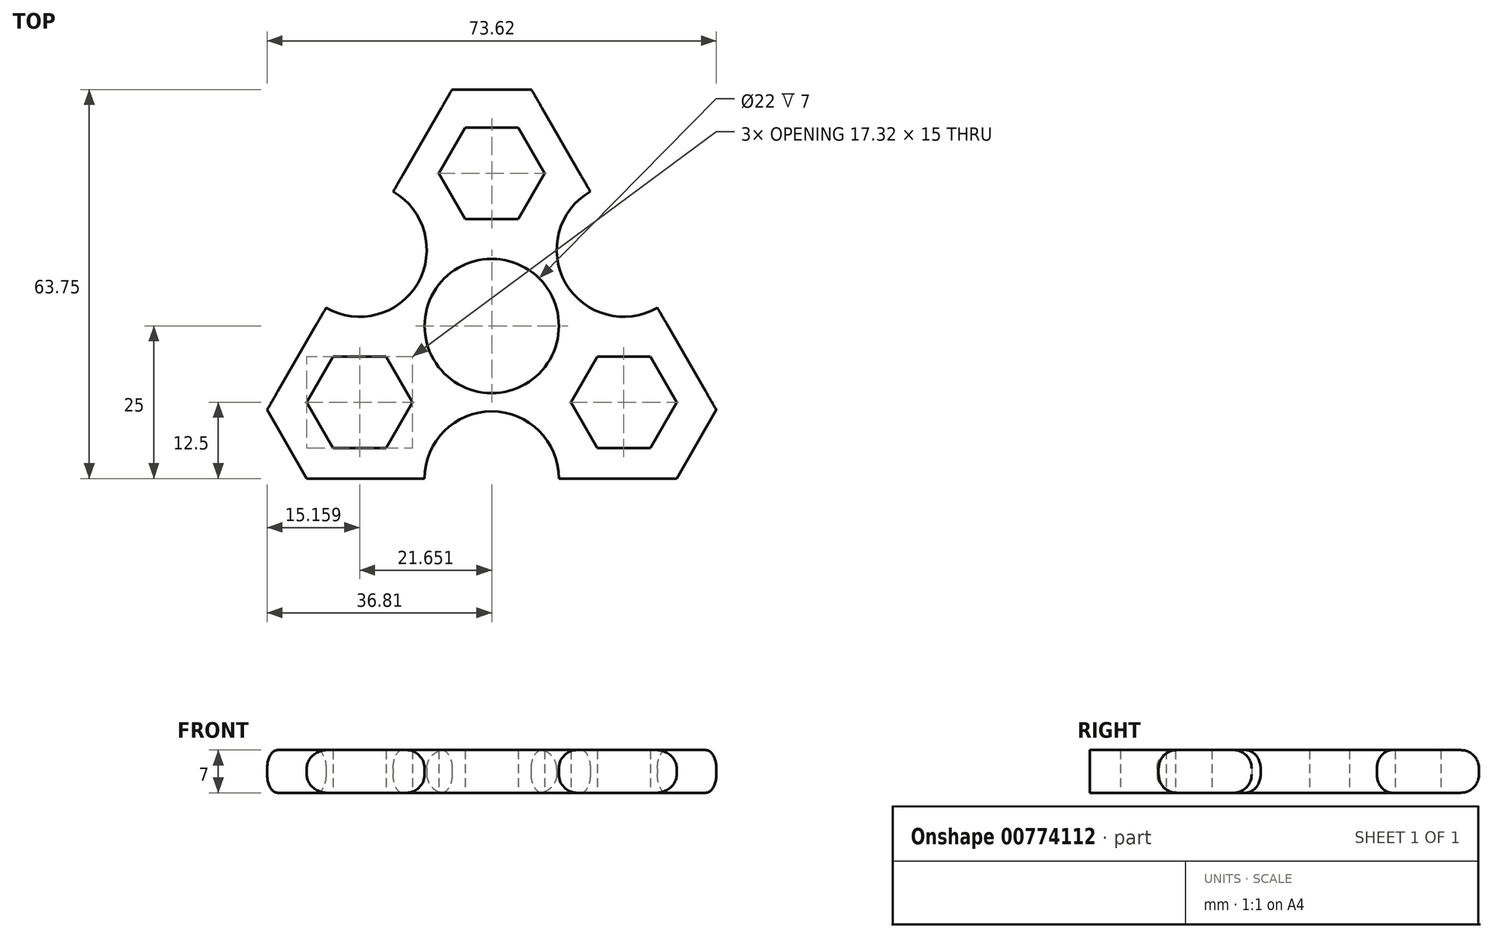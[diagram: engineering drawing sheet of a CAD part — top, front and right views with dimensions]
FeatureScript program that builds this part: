
annotation { "Feature Type Name" : "Feature", "Feature Type Description" : "" }
export const myFeature = defineFeature(function(context is Context, id is Id, definition is map)
    precondition{}
    {
        {
            var Q0;
            Q0=qCreatedBy(makeId("Top.planeOp"),FACE);
            var sketch = newSketch(context, id + "F0", { "sketchPlane" : qUnion([Q0])});
            skPoint(sketch, "E0", {"position": v(0, 0) * mm});
            skCircle(sketch, "E1", {"center": v(0, 0) * mm, "radius": 11 * mm});
            skCircle(sketch, "E2.cCircle", {"center": v(0, 0) * mm, "radius": 25 * mm, "construction": true});
            skLineSegment(sketch, "E2.0", {"start": v(43.3, -25) * mm, "end": v(-43.3, -25) * mm});
            skLineSegment(sketch, "E2.1", {"start": v(-43.3, -25) * mm, "end": v(0, 50) * mm});
            skLineSegment(sketch, "E2.2", {"start": v(0, 50) * mm, "end": v(43.3, -25) * mm});
            skPoint(sketch, "E2.0.midPoint", {"position": v(0, -25) * mm});
            skLineSegment(sketch, "E3", {"start": v(-43.3, -25) * mm, "end": v(0, 0) * mm});
            skLineSegment(sketch, "E4", {"start": v(0, 0) * mm, "end": v(43.3, -25) * mm});
            skLineSegment(sketch, "E5", {"start": v(0, 0) * mm, "end": v(0, 50) * mm});
            skCircle(sketch, "E6", {"center": v(-21.65, 12.5) * mm, "radius": 11 * mm});
            skCircle(sketch, "E7", {"center": v(21.65, 12.5) * mm, "radius": 11 * mm});
            skCircle(sketch, "E8", {"center": v(0, -25) * mm, "radius": 11 * mm});
            skLineSegment(sketch, "E9.0", {"start": v(25.98, -20) * mm, "end": v(17.32, -20) * mm});
            skLineSegment(sketch, "E9.1", {"start": v(17.32, -20) * mm, "end": v(13, -12.5) * mm});
            skLineSegment(sketch, "E9.2", {"start": v(13, -12.5) * mm, "end": v(17.32, -5) * mm});
            skLineSegment(sketch, "E9.3", {"start": v(17.32, -5) * mm, "end": v(25.98, -5) * mm});
            skLineSegment(sketch, "E9.4", {"start": v(25.98, -5) * mm, "end": v(30.31, -12.5) * mm});
            skLineSegment(sketch, "E9.5", {"start": v(30.31, -12.5) * mm, "end": v(25.98, -20) * mm});
            skPoint(sketch, "E10", {"position": v(21.65, -12.5) * mm});
            skPoint(sketch, "E10.positionSnap0", {"position": v(21.65, -20) * mm});
            skPoint(sketch, "E11", {"position": v(0, 25) * mm});
            skPoint(sketch, "E12", {"position": v(-21.65, -12.5) * mm});
            skLineSegment(sketch, "E13.0", {"start": v(4.33, 17.5) * mm, "end": v(-4.33, 17.5) * mm});
            skLineSegment(sketch, "E13.1", {"start": v(-4.33, 17.5) * mm, "end": v(-8.66, 25) * mm});
            skLineSegment(sketch, "E13.2", {"start": v(-8.66, 25) * mm, "end": v(-4.33, 32.5) * mm});
            skLineSegment(sketch, "E13.3", {"start": v(-4.33, 32.5) * mm, "end": v(4.33, 32.5) * mm});
            skLineSegment(sketch, "E13.4", {"start": v(4.33, 32.5) * mm, "end": v(8.66, 25) * mm});
            skLineSegment(sketch, "E13.5", {"start": v(8.66, 25) * mm, "end": v(4.33, 17.5) * mm});
            skPoint(sketch, "E13.0.midPoint", {"position": v(0, 17.5) * mm});
            skPoint(sketch, "E14.MirrorP", {"position": v(-21.65, -20) * mm});
            skLineSegment(sketch, "E15.MirrorCS", {"start": v(-25.98, -20) * mm, "end": v(-17.32, -20) * mm});
            skLineSegment(sketch, "E16.MirrorCS", {"start": v(-30.31, -12.5) * mm, "end": v(-25.98, -20) * mm});
            skLineSegment(sketch, "E17.MirrorCS", {"start": v(-25.98, -5) * mm, "end": v(-30.31, -12.5) * mm});
            skLineSegment(sketch, "E18.MirrorCS", {"start": v(-17.32, -5) * mm, "end": v(-25.98, -5) * mm});
            skLineSegment(sketch, "E19.MirrorCS", {"start": v(-13, -12.5) * mm, "end": v(-17.32, -5) * mm});
            skLineSegment(sketch, "E20.MirrorCS", {"start": v(-17.32, -20) * mm, "end": v(-13, -12.5) * mm});
            skCircle(sketch, "E21", {"center": v(0, 25) * mm, "radius": 7.5 * mm});
            skSolve(sketch);
        }
        {
            var Q0;
            {var subQ8=sQuery(id+"F0.wireOp",EDGE,"E3");var subQ11=sQuery(id+"F0.wireOp",EDGE,"E1");var subQ12=makeQuery(id+"F0.imprint","INTERSECT",VERTEX,{"derivedFrom":[subQ11,subQ8]});Q0=makeQuery(id+"F0.imprint","IMPRINT",FACE,{"disambiguationData":[TD([[makeQuery(id+"F0.imprint","IMPRINT",EDGE,{"disambiguationData":[TD([[subQ12,1.0]])],"derivedFrom":subQ11}),-1.0]])]});}
            var Q1;
            {var subQ0=sQuery(id+"F0.wireOp",EDGE,"E5");var subQ4=sQuery(id+"F0.wireOp",EDGE,"E1");var subQ5=makeQuery(id+"F0.imprint","INTERSECT",VERTEX,{"derivedFrom":[subQ4,subQ0]});Q1=makeQuery(id+"F0.imprint","IMPRINT",FACE,{"disambiguationData":[TD([[makeQuery(id+"F0.imprint","IMPRINT",EDGE,{"disambiguationData":[TD([[subQ5,1.0]])],"derivedFrom":subQ4}),-1.0]])]});}
            var Q2;
            {var subQ8=sQuery(id+"F0.wireOp",EDGE,"E3");var subQ11=sQuery(id+"F0.wireOp",EDGE,"E1");var subQ12=makeQuery(id+"F0.imprint","INTERSECT",VERTEX,{"derivedFrom":[subQ11,subQ8]});Q2=makeQuery(id+"F0.imprint","IMPRINT",FACE,{"disambiguationData":[TD([[makeQuery(id+"F0.imprint","IMPRINT",EDGE,{"disambiguationData":[TD([[subQ12,-1.0]])],"derivedFrom":subQ11}),-1.0]])]});}
            extrude(context, id + "F1", {"entities" : qUnion([Q0, Q1, Q2]), "depth" : 3.5 * mm, "offsetDistance" : 25 * mm, "hasSecondDirection" : true, "secondDirectionOppositeDirection" : true, "secondDirectionDepth" : 3.5 * mm});
        }
        {
            var Q0;
            Q0=makeQuery(id+"F1.opExtrude","SWEPT_EDGE",EDGE,{"disambiguationData":[OSD([sQuery(id+"F0.wireOp",EDGE,"E2.1"),sQuery(id+"F0.wireOp",EDGE,"E2.2"),sQuery(id+"F0.wireOp",EDGE,"E5")])]});
            var Q1;
            Q1=makeQuery(id+"F1.opExtrude","SWEPT_EDGE",EDGE,{"disambiguationData":[OSD([sQuery(id+"F0.wireOp",EDGE,"E2.0"),sQuery(id+"F0.wireOp",EDGE,"E2.2"),sQuery(id+"F0.wireOp",EDGE,"E4")])]});
            var Q2;
            Q2=makeQuery(id+"F1.opExtrude","SWEPT_EDGE",EDGE,{"disambiguationData":[OSD([sQuery(id+"F0.wireOp",EDGE,"E2.0"),sQuery(id+"F0.wireOp",EDGE,"E2.1"),sQuery(id+"F0.wireOp",EDGE,"E3")])]});
            chamfer(context, id + "F2", {"entities" : qUnion([Q0, Q1, Q2]), "width" : 7.5 * mm, "tangentPropagation" : true});
        }
        {
            var Q0;
            {var subQ0=sQuery(id+"F0.wireOp",EDGE,"E2.2");Q0=makeQuery(id+"F1.opExtrude","CAP_EDGE",EDGE,{"disambiguationData":[OSD([subQ0]),TDD([makeQuery(id+"F0.imprint","IMPRINT",EDGE,{"disambiguationData":[TD([[makeQuery(id+"F0.imprint","INTERSECT",VERTEX,{"disambiguationData":[OD(0.0)],"derivedFrom":[subQ0,sQuery(id+"F0.wireOp",EDGE,"E7")]}),1.0]])],"derivedFrom":subQ0})])],"isStart":false});}
            var Q1;
            Q1=makeQuery(id+"F1.opExtrude","CAP_EDGE",EDGE,{"disambiguationData":[OSD([sQuery(id+"F0.wireOp",EDGE,"E7")])],"isStart":false});
            var Q2;
            {var subQ0=sQuery(id+"F0.wireOp",EDGE,"E2.2");Q2=makeQuery(id+"F1.opExtrude","CAP_EDGE",EDGE,{"disambiguationData":[OSD([subQ0]),TDD([makeQuery(id+"F0.imprint","IMPRINT",EDGE,{"disambiguationData":[TD([[makeQuery(id+"F0.imprint","INTERSECT",VERTEX,{"disambiguationData":[OD(1.0)],"derivedFrom":[subQ0,sQuery(id+"F0.wireOp",EDGE,"E7")]}),-1.0]])],"derivedFrom":subQ0})])],"isStart":false});}
            var Q3;
            {var subQ0=sQuery(id+"F0.wireOp",EDGE,"E2.2");var subQ1=sQuery(id+"F0.wireOp",EDGE,"E2.0");Q3=makeQuery(id+"F2.opChamfer","BLEND_EDGE",EDGE,{"blendedFrom":[makeQuery(id+"F1.opExtrude","SWEPT_EDGE",EDGE,{"disambiguationData":[OSD([subQ1,subQ0,sQuery(id+"F0.wireOp",EDGE,"E4")])]}),makeQuery(id+"F1.opExtrude","CAP_FACE",FACE,{"disambiguationData":[OSD([sQuery(id+"F0.wireOp",EDGE,"E1"),subQ1,sQuery(id+"F0.wireOp",EDGE,"E2.1"),subQ0,sQuery(id+"F0.wireOp",EDGE,"E6"),sQuery(id+"F0.wireOp",EDGE,"E7"),sQuery(id+"F0.wireOp",EDGE,"E8"),sQuery(id+"F0.wireOp",EDGE,"E9.0"),sQuery(id+"F0.wireOp",EDGE,"E9.1"),sQuery(id+"F0.wireOp",EDGE,"E9.2"),sQuery(id+"F0.wireOp",EDGE,"E9.3"),sQuery(id+"F0.wireOp",EDGE,"E9.4"),sQuery(id+"F0.wireOp",EDGE,"E9.5"),sQuery(id+"F0.wireOp",EDGE,"E13.0"),sQuery(id+"F0.wireOp",EDGE,"E13.1"),sQuery(id+"F0.wireOp",EDGE,"E13.2"),sQuery(id+"F0.wireOp",EDGE,"E13.3"),sQuery(id+"F0.wireOp",EDGE,"E13.4"),sQuery(id+"F0.wireOp",EDGE,"E13.5"),sQuery(id+"F0.wireOp",EDGE,"E15.MirrorCS"),sQuery(id+"F0.wireOp",EDGE,"E16.MirrorCS"),sQuery(id+"F0.wireOp",EDGE,"E17.MirrorCS"),sQuery(id+"F0.wireOp",EDGE,"E18.MirrorCS"),sQuery(id+"F0.wireOp",EDGE,"E19.MirrorCS"),sQuery(id+"F0.wireOp",EDGE,"E20.MirrorCS")])],"isStart":false})],"blendedInto":[makeQuery(id+"F1.opExtrude","CAP_FACE",FACE,{"disambiguationData":[OSD([sQuery(id+"F0.wireOp",EDGE,"E1"),subQ1,sQuery(id+"F0.wireOp",EDGE,"E2.1"),subQ0,sQuery(id+"F0.wireOp",EDGE,"E6"),sQuery(id+"F0.wireOp",EDGE,"E7"),sQuery(id+"F0.wireOp",EDGE,"E8"),sQuery(id+"F0.wireOp",EDGE,"E9.0"),sQuery(id+"F0.wireOp",EDGE,"E9.1"),sQuery(id+"F0.wireOp",EDGE,"E9.2"),sQuery(id+"F0.wireOp",EDGE,"E9.3"),sQuery(id+"F0.wireOp",EDGE,"E9.4"),sQuery(id+"F0.wireOp",EDGE,"E9.5"),sQuery(id+"F0.wireOp",EDGE,"E13.0"),sQuery(id+"F0.wireOp",EDGE,"E13.1"),sQuery(id+"F0.wireOp",EDGE,"E13.2"),sQuery(id+"F0.wireOp",EDGE,"E13.3"),sQuery(id+"F0.wireOp",EDGE,"E13.4"),sQuery(id+"F0.wireOp",EDGE,"E13.5"),sQuery(id+"F0.wireOp",EDGE,"E15.MirrorCS"),sQuery(id+"F0.wireOp",EDGE,"E16.MirrorCS"),sQuery(id+"F0.wireOp",EDGE,"E17.MirrorCS"),sQuery(id+"F0.wireOp",EDGE,"E18.MirrorCS"),sQuery(id+"F0.wireOp",EDGE,"E19.MirrorCS"),sQuery(id+"F0.wireOp",EDGE,"E20.MirrorCS")])],"isStart":false})]});}
            var Q4;
            {var subQ0=sQuery(id+"F0.wireOp",EDGE,"E2.0");Q4=makeQuery(id+"F1.opExtrude","CAP_EDGE",EDGE,{"disambiguationData":[OSD([subQ0]),TDD([makeQuery(id+"F0.imprint","IMPRINT",EDGE,{"disambiguationData":[TD([[makeQuery(id+"F0.imprint","INTERSECT",VERTEX,{"disambiguationData":[OD(0.0)],"derivedFrom":[subQ0,sQuery(id+"F0.wireOp",EDGE,"E8")]}),1.0]])],"derivedFrom":subQ0})])],"isStart":false});}
            var Q5;
            Q5=makeQuery(id+"F1.opExtrude","CAP_EDGE",EDGE,{"disambiguationData":[OSD([sQuery(id+"F0.wireOp",EDGE,"E8")])],"isStart":false});
            var Q6;
            {var subQ0=sQuery(id+"F0.wireOp",EDGE,"E2.0");Q6=makeQuery(id+"F1.opExtrude","CAP_EDGE",EDGE,{"disambiguationData":[OSD([subQ0]),TDD([makeQuery(id+"F0.imprint","IMPRINT",EDGE,{"disambiguationData":[TD([[makeQuery(id+"F0.imprint","INTERSECT",VERTEX,{"disambiguationData":[OD(1.0)],"derivedFrom":[subQ0,sQuery(id+"F0.wireOp",EDGE,"E8")]}),-1.0]])],"derivedFrom":subQ0})])],"isStart":false});}
            var Q7;
            {var subQ0=sQuery(id+"F0.wireOp",EDGE,"E2.1");var subQ1=sQuery(id+"F0.wireOp",EDGE,"E2.0");Q7=makeQuery(id+"F2.opChamfer","BLEND_EDGE",EDGE,{"blendedFrom":[makeQuery(id+"F1.opExtrude","SWEPT_EDGE",EDGE,{"disambiguationData":[OSD([subQ1,subQ0,sQuery(id+"F0.wireOp",EDGE,"E3")])]}),makeQuery(id+"F1.opExtrude","CAP_FACE",FACE,{"disambiguationData":[OSD([sQuery(id+"F0.wireOp",EDGE,"E1"),subQ1,subQ0,sQuery(id+"F0.wireOp",EDGE,"E2.2"),sQuery(id+"F0.wireOp",EDGE,"E6"),sQuery(id+"F0.wireOp",EDGE,"E7"),sQuery(id+"F0.wireOp",EDGE,"E8"),sQuery(id+"F0.wireOp",EDGE,"E9.0"),sQuery(id+"F0.wireOp",EDGE,"E9.1"),sQuery(id+"F0.wireOp",EDGE,"E9.2"),sQuery(id+"F0.wireOp",EDGE,"E9.3"),sQuery(id+"F0.wireOp",EDGE,"E9.4"),sQuery(id+"F0.wireOp",EDGE,"E9.5"),sQuery(id+"F0.wireOp",EDGE,"E13.0"),sQuery(id+"F0.wireOp",EDGE,"E13.1"),sQuery(id+"F0.wireOp",EDGE,"E13.2"),sQuery(id+"F0.wireOp",EDGE,"E13.3"),sQuery(id+"F0.wireOp",EDGE,"E13.4"),sQuery(id+"F0.wireOp",EDGE,"E13.5"),sQuery(id+"F0.wireOp",EDGE,"E15.MirrorCS"),sQuery(id+"F0.wireOp",EDGE,"E16.MirrorCS"),sQuery(id+"F0.wireOp",EDGE,"E17.MirrorCS"),sQuery(id+"F0.wireOp",EDGE,"E18.MirrorCS"),sQuery(id+"F0.wireOp",EDGE,"E19.MirrorCS"),sQuery(id+"F0.wireOp",EDGE,"E20.MirrorCS")])],"isStart":false})],"blendedInto":[makeQuery(id+"F1.opExtrude","CAP_FACE",FACE,{"disambiguationData":[OSD([sQuery(id+"F0.wireOp",EDGE,"E1"),subQ1,subQ0,sQuery(id+"F0.wireOp",EDGE,"E2.2"),sQuery(id+"F0.wireOp",EDGE,"E6"),sQuery(id+"F0.wireOp",EDGE,"E7"),sQuery(id+"F0.wireOp",EDGE,"E8"),sQuery(id+"F0.wireOp",EDGE,"E9.0"),sQuery(id+"F0.wireOp",EDGE,"E9.1"),sQuery(id+"F0.wireOp",EDGE,"E9.2"),sQuery(id+"F0.wireOp",EDGE,"E9.3"),sQuery(id+"F0.wireOp",EDGE,"E9.4"),sQuery(id+"F0.wireOp",EDGE,"E9.5"),sQuery(id+"F0.wireOp",EDGE,"E13.0"),sQuery(id+"F0.wireOp",EDGE,"E13.1"),sQuery(id+"F0.wireOp",EDGE,"E13.2"),sQuery(id+"F0.wireOp",EDGE,"E13.3"),sQuery(id+"F0.wireOp",EDGE,"E13.4"),sQuery(id+"F0.wireOp",EDGE,"E13.5"),sQuery(id+"F0.wireOp",EDGE,"E15.MirrorCS"),sQuery(id+"F0.wireOp",EDGE,"E16.MirrorCS"),sQuery(id+"F0.wireOp",EDGE,"E17.MirrorCS"),sQuery(id+"F0.wireOp",EDGE,"E18.MirrorCS"),sQuery(id+"F0.wireOp",EDGE,"E19.MirrorCS"),sQuery(id+"F0.wireOp",EDGE,"E20.MirrorCS")])],"isStart":false})]});}
            var Q8;
            {var subQ0=sQuery(id+"F0.wireOp",EDGE,"E2.1");Q8=makeQuery(id+"F1.opExtrude","CAP_EDGE",EDGE,{"disambiguationData":[OSD([subQ0]),TDD([makeQuery(id+"F0.imprint","IMPRINT",EDGE,{"disambiguationData":[TD([[makeQuery(id+"F0.imprint","INTERSECT",VERTEX,{"disambiguationData":[OD(0.0)],"derivedFrom":[subQ0,sQuery(id+"F0.wireOp",EDGE,"E6")]}),1.0]])],"derivedFrom":subQ0})])],"isStart":false});}
            var Q9;
            Q9=makeQuery(id+"F1.opExtrude","CAP_EDGE",EDGE,{"disambiguationData":[OSD([sQuery(id+"F0.wireOp",EDGE,"E6")])],"isStart":false});
            var Q10;
            {var subQ0=sQuery(id+"F0.wireOp",EDGE,"E2.1");Q10=makeQuery(id+"F1.opExtrude","CAP_EDGE",EDGE,{"disambiguationData":[OSD([subQ0]),TDD([makeQuery(id+"F0.imprint","IMPRINT",EDGE,{"disambiguationData":[TD([[makeQuery(id+"F0.imprint","INTERSECT",VERTEX,{"disambiguationData":[OD(1.0)],"derivedFrom":[subQ0,sQuery(id+"F0.wireOp",EDGE,"E6")]}),-1.0]])],"derivedFrom":subQ0})])],"isStart":false});}
            var Q11;
            {var subQ0=sQuery(id+"F0.wireOp",EDGE,"E2.2");var subQ1=sQuery(id+"F0.wireOp",EDGE,"E2.1");Q11=makeQuery(id+"F2.opChamfer","BLEND_EDGE",EDGE,{"blendedFrom":[makeQuery(id+"F1.opExtrude","SWEPT_EDGE",EDGE,{"disambiguationData":[OSD([subQ1,subQ0,sQuery(id+"F0.wireOp",EDGE,"E5")])]}),makeQuery(id+"F1.opExtrude","CAP_FACE",FACE,{"disambiguationData":[OSD([sQuery(id+"F0.wireOp",EDGE,"E1"),sQuery(id+"F0.wireOp",EDGE,"E2.0"),subQ1,subQ0,sQuery(id+"F0.wireOp",EDGE,"E6"),sQuery(id+"F0.wireOp",EDGE,"E7"),sQuery(id+"F0.wireOp",EDGE,"E8"),sQuery(id+"F0.wireOp",EDGE,"E9.0"),sQuery(id+"F0.wireOp",EDGE,"E9.1"),sQuery(id+"F0.wireOp",EDGE,"E9.2"),sQuery(id+"F0.wireOp",EDGE,"E9.3"),sQuery(id+"F0.wireOp",EDGE,"E9.4"),sQuery(id+"F0.wireOp",EDGE,"E9.5"),sQuery(id+"F0.wireOp",EDGE,"E13.0"),sQuery(id+"F0.wireOp",EDGE,"E13.1"),sQuery(id+"F0.wireOp",EDGE,"E13.2"),sQuery(id+"F0.wireOp",EDGE,"E13.3"),sQuery(id+"F0.wireOp",EDGE,"E13.4"),sQuery(id+"F0.wireOp",EDGE,"E13.5"),sQuery(id+"F0.wireOp",EDGE,"E15.MirrorCS"),sQuery(id+"F0.wireOp",EDGE,"E16.MirrorCS"),sQuery(id+"F0.wireOp",EDGE,"E17.MirrorCS"),sQuery(id+"F0.wireOp",EDGE,"E18.MirrorCS"),sQuery(id+"F0.wireOp",EDGE,"E19.MirrorCS"),sQuery(id+"F0.wireOp",EDGE,"E20.MirrorCS")])],"isStart":false})],"blendedInto":[makeQuery(id+"F1.opExtrude","CAP_FACE",FACE,{"disambiguationData":[OSD([sQuery(id+"F0.wireOp",EDGE,"E1"),sQuery(id+"F0.wireOp",EDGE,"E2.0"),subQ1,subQ0,sQuery(id+"F0.wireOp",EDGE,"E6"),sQuery(id+"F0.wireOp",EDGE,"E7"),sQuery(id+"F0.wireOp",EDGE,"E8"),sQuery(id+"F0.wireOp",EDGE,"E9.0"),sQuery(id+"F0.wireOp",EDGE,"E9.1"),sQuery(id+"F0.wireOp",EDGE,"E9.2"),sQuery(id+"F0.wireOp",EDGE,"E9.3"),sQuery(id+"F0.wireOp",EDGE,"E9.4"),sQuery(id+"F0.wireOp",EDGE,"E9.5"),sQuery(id+"F0.wireOp",EDGE,"E13.0"),sQuery(id+"F0.wireOp",EDGE,"E13.1"),sQuery(id+"F0.wireOp",EDGE,"E13.2"),sQuery(id+"F0.wireOp",EDGE,"E13.3"),sQuery(id+"F0.wireOp",EDGE,"E13.4"),sQuery(id+"F0.wireOp",EDGE,"E13.5"),sQuery(id+"F0.wireOp",EDGE,"E15.MirrorCS"),sQuery(id+"F0.wireOp",EDGE,"E16.MirrorCS"),sQuery(id+"F0.wireOp",EDGE,"E17.MirrorCS"),sQuery(id+"F0.wireOp",EDGE,"E18.MirrorCS"),sQuery(id+"F0.wireOp",EDGE,"E19.MirrorCS"),sQuery(id+"F0.wireOp",EDGE,"E20.MirrorCS")])],"isStart":false})]});}
            fillet(context, id + "F3", {"entities" : qUnion([Q0, Q1, Q2, Q3, Q4, Q5, Q6, Q7, Q8, Q9, Q10, Q11]), "radius" : 3 * mm, "tangentPropagation" : true, "allowEdgeOverflow" : false});
        }
        {
            var Q0;
            {var subQ0=sQuery(id+"F0.wireOp",EDGE,"E2.1");var subQ1=sQuery(id+"F0.wireOp",EDGE,"E2.0");Q0=makeQuery(id+"F2.opChamfer","BLEND_EDGE",EDGE,{"blendedFrom":[makeQuery(id+"F1.opExtrude","SWEPT_EDGE",EDGE,{"disambiguationData":[OSD([subQ1,subQ0,sQuery(id+"F0.wireOp",EDGE,"E3")])]}),makeQuery(id+"F1.opExtrude","CAP_FACE",FACE,{"disambiguationData":[OSD([sQuery(id+"F0.wireOp",EDGE,"E1"),subQ1,subQ0,sQuery(id+"F0.wireOp",EDGE,"E2.2"),sQuery(id+"F0.wireOp",EDGE,"E6"),sQuery(id+"F0.wireOp",EDGE,"E7"),sQuery(id+"F0.wireOp",EDGE,"E8"),sQuery(id+"F0.wireOp",EDGE,"E9.0"),sQuery(id+"F0.wireOp",EDGE,"E9.1"),sQuery(id+"F0.wireOp",EDGE,"E9.2"),sQuery(id+"F0.wireOp",EDGE,"E9.3"),sQuery(id+"F0.wireOp",EDGE,"E9.4"),sQuery(id+"F0.wireOp",EDGE,"E9.5"),sQuery(id+"F0.wireOp",EDGE,"E13.0"),sQuery(id+"F0.wireOp",EDGE,"E13.1"),sQuery(id+"F0.wireOp",EDGE,"E13.2"),sQuery(id+"F0.wireOp",EDGE,"E13.3"),sQuery(id+"F0.wireOp",EDGE,"E13.4"),sQuery(id+"F0.wireOp",EDGE,"E13.5"),sQuery(id+"F0.wireOp",EDGE,"E15.MirrorCS"),sQuery(id+"F0.wireOp",EDGE,"E16.MirrorCS"),sQuery(id+"F0.wireOp",EDGE,"E17.MirrorCS"),sQuery(id+"F0.wireOp",EDGE,"E18.MirrorCS"),sQuery(id+"F0.wireOp",EDGE,"E19.MirrorCS"),sQuery(id+"F0.wireOp",EDGE,"E20.MirrorCS")])],"isStart":true})],"blendedInto":[makeQuery(id+"F1.opExtrude","CAP_FACE",FACE,{"disambiguationData":[OSD([sQuery(id+"F0.wireOp",EDGE,"E1"),subQ1,subQ0,sQuery(id+"F0.wireOp",EDGE,"E2.2"),sQuery(id+"F0.wireOp",EDGE,"E6"),sQuery(id+"F0.wireOp",EDGE,"E7"),sQuery(id+"F0.wireOp",EDGE,"E8"),sQuery(id+"F0.wireOp",EDGE,"E9.0"),sQuery(id+"F0.wireOp",EDGE,"E9.1"),sQuery(id+"F0.wireOp",EDGE,"E9.2"),sQuery(id+"F0.wireOp",EDGE,"E9.3"),sQuery(id+"F0.wireOp",EDGE,"E9.4"),sQuery(id+"F0.wireOp",EDGE,"E9.5"),sQuery(id+"F0.wireOp",EDGE,"E13.0"),sQuery(id+"F0.wireOp",EDGE,"E13.1"),sQuery(id+"F0.wireOp",EDGE,"E13.2"),sQuery(id+"F0.wireOp",EDGE,"E13.3"),sQuery(id+"F0.wireOp",EDGE,"E13.4"),sQuery(id+"F0.wireOp",EDGE,"E13.5"),sQuery(id+"F0.wireOp",EDGE,"E15.MirrorCS"),sQuery(id+"F0.wireOp",EDGE,"E16.MirrorCS"),sQuery(id+"F0.wireOp",EDGE,"E17.MirrorCS"),sQuery(id+"F0.wireOp",EDGE,"E18.MirrorCS"),sQuery(id+"F0.wireOp",EDGE,"E19.MirrorCS"),sQuery(id+"F0.wireOp",EDGE,"E20.MirrorCS")])],"isStart":true})]});}
            var Q1;
            {var subQ0=sQuery(id+"F0.wireOp",EDGE,"E2.2");var subQ1=sQuery(id+"F0.wireOp",EDGE,"E2.0");Q1=makeQuery(id+"F2.opChamfer","BLEND_EDGE",EDGE,{"blendedFrom":[makeQuery(id+"F1.opExtrude","SWEPT_EDGE",EDGE,{"disambiguationData":[OSD([subQ1,subQ0,sQuery(id+"F0.wireOp",EDGE,"E4")])]}),makeQuery(id+"F1.opExtrude","CAP_FACE",FACE,{"disambiguationData":[OSD([sQuery(id+"F0.wireOp",EDGE,"E1"),subQ1,sQuery(id+"F0.wireOp",EDGE,"E2.1"),subQ0,sQuery(id+"F0.wireOp",EDGE,"E6"),sQuery(id+"F0.wireOp",EDGE,"E7"),sQuery(id+"F0.wireOp",EDGE,"E8"),sQuery(id+"F0.wireOp",EDGE,"E9.0"),sQuery(id+"F0.wireOp",EDGE,"E9.1"),sQuery(id+"F0.wireOp",EDGE,"E9.2"),sQuery(id+"F0.wireOp",EDGE,"E9.3"),sQuery(id+"F0.wireOp",EDGE,"E9.4"),sQuery(id+"F0.wireOp",EDGE,"E9.5"),sQuery(id+"F0.wireOp",EDGE,"E13.0"),sQuery(id+"F0.wireOp",EDGE,"E13.1"),sQuery(id+"F0.wireOp",EDGE,"E13.2"),sQuery(id+"F0.wireOp",EDGE,"E13.3"),sQuery(id+"F0.wireOp",EDGE,"E13.4"),sQuery(id+"F0.wireOp",EDGE,"E13.5"),sQuery(id+"F0.wireOp",EDGE,"E15.MirrorCS"),sQuery(id+"F0.wireOp",EDGE,"E16.MirrorCS"),sQuery(id+"F0.wireOp",EDGE,"E17.MirrorCS"),sQuery(id+"F0.wireOp",EDGE,"E18.MirrorCS"),sQuery(id+"F0.wireOp",EDGE,"E19.MirrorCS"),sQuery(id+"F0.wireOp",EDGE,"E20.MirrorCS")])],"isStart":true})],"blendedInto":[makeQuery(id+"F1.opExtrude","CAP_FACE",FACE,{"disambiguationData":[OSD([sQuery(id+"F0.wireOp",EDGE,"E1"),subQ1,sQuery(id+"F0.wireOp",EDGE,"E2.1"),subQ0,sQuery(id+"F0.wireOp",EDGE,"E6"),sQuery(id+"F0.wireOp",EDGE,"E7"),sQuery(id+"F0.wireOp",EDGE,"E8"),sQuery(id+"F0.wireOp",EDGE,"E9.0"),sQuery(id+"F0.wireOp",EDGE,"E9.1"),sQuery(id+"F0.wireOp",EDGE,"E9.2"),sQuery(id+"F0.wireOp",EDGE,"E9.3"),sQuery(id+"F0.wireOp",EDGE,"E9.4"),sQuery(id+"F0.wireOp",EDGE,"E9.5"),sQuery(id+"F0.wireOp",EDGE,"E13.0"),sQuery(id+"F0.wireOp",EDGE,"E13.1"),sQuery(id+"F0.wireOp",EDGE,"E13.2"),sQuery(id+"F0.wireOp",EDGE,"E13.3"),sQuery(id+"F0.wireOp",EDGE,"E13.4"),sQuery(id+"F0.wireOp",EDGE,"E13.5"),sQuery(id+"F0.wireOp",EDGE,"E15.MirrorCS"),sQuery(id+"F0.wireOp",EDGE,"E16.MirrorCS"),sQuery(id+"F0.wireOp",EDGE,"E17.MirrorCS"),sQuery(id+"F0.wireOp",EDGE,"E18.MirrorCS"),sQuery(id+"F0.wireOp",EDGE,"E19.MirrorCS"),sQuery(id+"F0.wireOp",EDGE,"E20.MirrorCS")])],"isStart":true})]});}
            var Q2;
            {var subQ0=sQuery(id+"F0.wireOp",EDGE,"E2.2");var subQ1=sQuery(id+"F0.wireOp",EDGE,"E2.1");Q2=makeQuery(id+"F2.opChamfer","BLEND_EDGE",EDGE,{"blendedFrom":[makeQuery(id+"F1.opExtrude","SWEPT_EDGE",EDGE,{"disambiguationData":[OSD([subQ1,subQ0,sQuery(id+"F0.wireOp",EDGE,"E5")])]}),makeQuery(id+"F1.opExtrude","CAP_FACE",FACE,{"disambiguationData":[OSD([sQuery(id+"F0.wireOp",EDGE,"E1"),sQuery(id+"F0.wireOp",EDGE,"E2.0"),subQ1,subQ0,sQuery(id+"F0.wireOp",EDGE,"E6"),sQuery(id+"F0.wireOp",EDGE,"E7"),sQuery(id+"F0.wireOp",EDGE,"E8"),sQuery(id+"F0.wireOp",EDGE,"E9.0"),sQuery(id+"F0.wireOp",EDGE,"E9.1"),sQuery(id+"F0.wireOp",EDGE,"E9.2"),sQuery(id+"F0.wireOp",EDGE,"E9.3"),sQuery(id+"F0.wireOp",EDGE,"E9.4"),sQuery(id+"F0.wireOp",EDGE,"E9.5"),sQuery(id+"F0.wireOp",EDGE,"E13.0"),sQuery(id+"F0.wireOp",EDGE,"E13.1"),sQuery(id+"F0.wireOp",EDGE,"E13.2"),sQuery(id+"F0.wireOp",EDGE,"E13.3"),sQuery(id+"F0.wireOp",EDGE,"E13.4"),sQuery(id+"F0.wireOp",EDGE,"E13.5"),sQuery(id+"F0.wireOp",EDGE,"E15.MirrorCS"),sQuery(id+"F0.wireOp",EDGE,"E16.MirrorCS"),sQuery(id+"F0.wireOp",EDGE,"E17.MirrorCS"),sQuery(id+"F0.wireOp",EDGE,"E18.MirrorCS"),sQuery(id+"F0.wireOp",EDGE,"E19.MirrorCS"),sQuery(id+"F0.wireOp",EDGE,"E20.MirrorCS")])],"isStart":true})],"blendedInto":[makeQuery(id+"F1.opExtrude","CAP_FACE",FACE,{"disambiguationData":[OSD([sQuery(id+"F0.wireOp",EDGE,"E1"),sQuery(id+"F0.wireOp",EDGE,"E2.0"),subQ1,subQ0,sQuery(id+"F0.wireOp",EDGE,"E6"),sQuery(id+"F0.wireOp",EDGE,"E7"),sQuery(id+"F0.wireOp",EDGE,"E8"),sQuery(id+"F0.wireOp",EDGE,"E9.0"),sQuery(id+"F0.wireOp",EDGE,"E9.1"),sQuery(id+"F0.wireOp",EDGE,"E9.2"),sQuery(id+"F0.wireOp",EDGE,"E9.3"),sQuery(id+"F0.wireOp",EDGE,"E9.4"),sQuery(id+"F0.wireOp",EDGE,"E9.5"),sQuery(id+"F0.wireOp",EDGE,"E13.0"),sQuery(id+"F0.wireOp",EDGE,"E13.1"),sQuery(id+"F0.wireOp",EDGE,"E13.2"),sQuery(id+"F0.wireOp",EDGE,"E13.3"),sQuery(id+"F0.wireOp",EDGE,"E13.4"),sQuery(id+"F0.wireOp",EDGE,"E13.5"),sQuery(id+"F0.wireOp",EDGE,"E15.MirrorCS"),sQuery(id+"F0.wireOp",EDGE,"E16.MirrorCS"),sQuery(id+"F0.wireOp",EDGE,"E17.MirrorCS"),sQuery(id+"F0.wireOp",EDGE,"E18.MirrorCS"),sQuery(id+"F0.wireOp",EDGE,"E19.MirrorCS"),sQuery(id+"F0.wireOp",EDGE,"E20.MirrorCS")])],"isStart":true})]});}
            var Q3;
            {var subQ0=sQuery(id+"F0.wireOp",EDGE,"E2.1");Q3=makeQuery(id+"F1.opExtrude","CAP_EDGE",EDGE,{"disambiguationData":[OSD([subQ0]),TDD([makeQuery(id+"F0.imprint","IMPRINT",EDGE,{"disambiguationData":[TD([[makeQuery(id+"F0.imprint","INTERSECT",VERTEX,{"disambiguationData":[OD(1.0)],"derivedFrom":[subQ0,sQuery(id+"F0.wireOp",EDGE,"E6")]}),-1.0]])],"derivedFrom":subQ0})])],"isStart":true});}
            var Q4;
            Q4=makeQuery(id+"F1.opExtrude","CAP_EDGE",EDGE,{"disambiguationData":[OSD([sQuery(id+"F0.wireOp",EDGE,"E6")])],"isStart":true});
            var Q5;
            {var subQ0=sQuery(id+"F0.wireOp",EDGE,"E2.1");Q5=makeQuery(id+"F1.opExtrude","CAP_EDGE",EDGE,{"disambiguationData":[OSD([subQ0]),TDD([makeQuery(id+"F0.imprint","IMPRINT",EDGE,{"disambiguationData":[TD([[makeQuery(id+"F0.imprint","INTERSECT",VERTEX,{"disambiguationData":[OD(0.0)],"derivedFrom":[subQ0,sQuery(id+"F0.wireOp",EDGE,"E6")]}),1.0]])],"derivedFrom":subQ0})])],"isStart":true});}
            var Q6;
            {var subQ0=sQuery(id+"F0.wireOp",EDGE,"E2.0");Q6=makeQuery(id+"F1.opExtrude","CAP_EDGE",EDGE,{"disambiguationData":[OSD([subQ0]),TDD([makeQuery(id+"F0.imprint","IMPRINT",EDGE,{"disambiguationData":[TD([[makeQuery(id+"F0.imprint","INTERSECT",VERTEX,{"disambiguationData":[OD(1.0)],"derivedFrom":[subQ0,sQuery(id+"F0.wireOp",EDGE,"E8")]}),-1.0]])],"derivedFrom":subQ0})])],"isStart":true});}
            var Q7;
            Q7=makeQuery(id+"F1.opExtrude","CAP_EDGE",EDGE,{"disambiguationData":[OSD([sQuery(id+"F0.wireOp",EDGE,"E8")])],"isStart":true});
            var Q8;
            {var subQ0=sQuery(id+"F0.wireOp",EDGE,"E2.0");Q8=makeQuery(id+"F1.opExtrude","CAP_EDGE",EDGE,{"disambiguationData":[OSD([subQ0]),TDD([makeQuery(id+"F0.imprint","IMPRINT",EDGE,{"disambiguationData":[TD([[makeQuery(id+"F0.imprint","INTERSECT",VERTEX,{"disambiguationData":[OD(0.0)],"derivedFrom":[subQ0,sQuery(id+"F0.wireOp",EDGE,"E8")]}),1.0]])],"derivedFrom":subQ0})])],"isStart":true});}
            var Q9;
            {var subQ0=sQuery(id+"F0.wireOp",EDGE,"E2.2");Q9=makeQuery(id+"F1.opExtrude","CAP_EDGE",EDGE,{"disambiguationData":[OSD([subQ0]),TDD([makeQuery(id+"F0.imprint","IMPRINT",EDGE,{"disambiguationData":[TD([[makeQuery(id+"F0.imprint","INTERSECT",VERTEX,{"disambiguationData":[OD(1.0)],"derivedFrom":[subQ0,sQuery(id+"F0.wireOp",EDGE,"E7")]}),-1.0]])],"derivedFrom":subQ0})])],"isStart":true});}
            var Q10;
            Q10=makeQuery(id+"F1.opExtrude","CAP_EDGE",EDGE,{"disambiguationData":[OSD([sQuery(id+"F0.wireOp",EDGE,"E7")])],"isStart":true});
            var Q11;
            {var subQ0=sQuery(id+"F0.wireOp",EDGE,"E2.2");Q11=makeQuery(id+"F1.opExtrude","CAP_EDGE",EDGE,{"disambiguationData":[OSD([subQ0]),TDD([makeQuery(id+"F0.imprint","IMPRINT",EDGE,{"disambiguationData":[TD([[makeQuery(id+"F0.imprint","INTERSECT",VERTEX,{"disambiguationData":[OD(0.0)],"derivedFrom":[subQ0,sQuery(id+"F0.wireOp",EDGE,"E7")]}),1.0]])],"derivedFrom":subQ0})])],"isStart":true});}
            fillet(context, id + "F4", {"entities" : qUnion([Q0, Q1, Q2, Q3, Q4, Q5, Q6, Q7, Q8, Q9, Q10, Q11]), "radius" : 3 * mm, "tangentPropagation" : true, "allowEdgeOverflow" : false});
        }
    });
